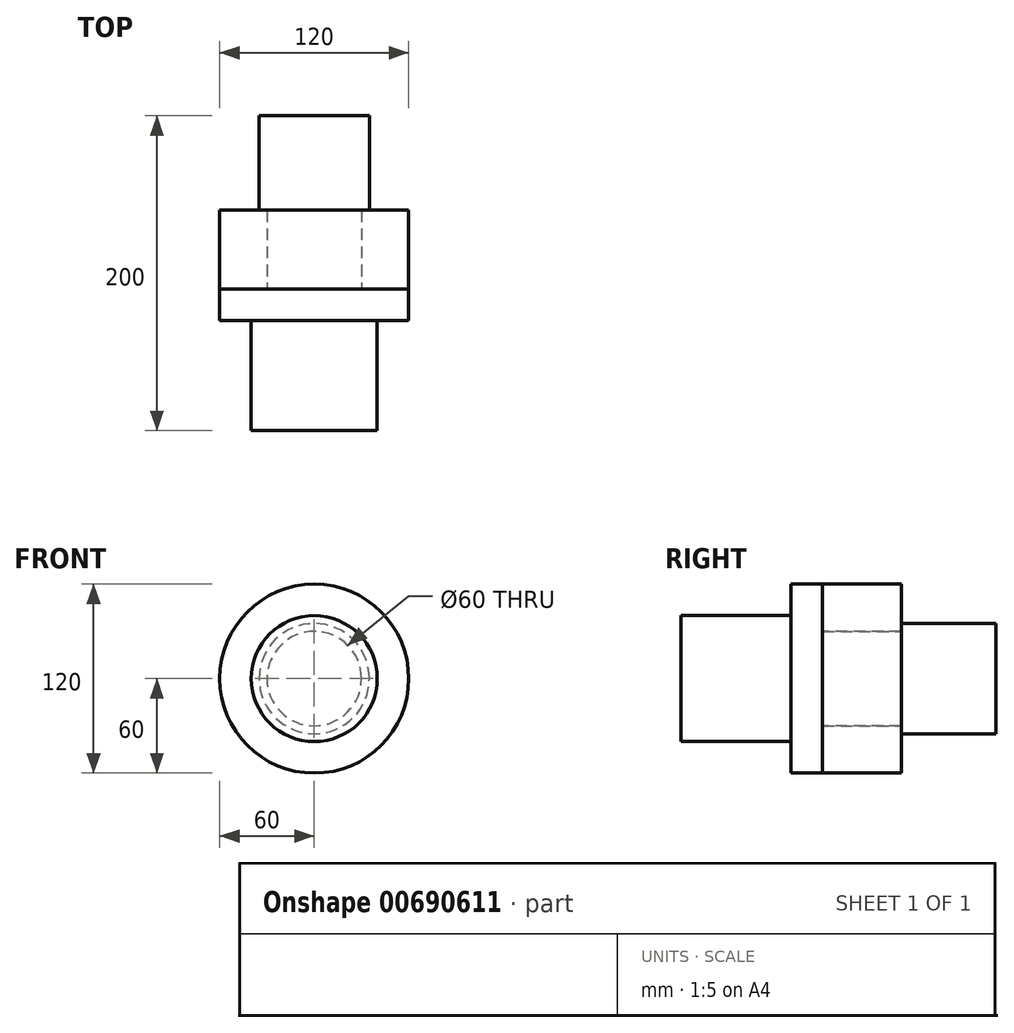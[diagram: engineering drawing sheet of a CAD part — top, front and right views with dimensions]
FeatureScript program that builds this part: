
annotation { "Feature Type Name" : "Feature", "Feature Type Description" : "" }
export const myFeature = defineFeature(function(context is Context, id is Id, definition is map)
    precondition{}
    {
        {
            var Q0;
            Q0=qCreatedBy(makeId("Right.planeOp"),FACE);
            var sketch = newSketch(context, id + "F0", { "sketchPlane" : qUnion([Q0])});
            skLineSegment(sketch, "E0", {"start": v(0, 0) * mm, "end": v(0, 40) * mm});
            skLineSegment(sketch, "E1", {"start": v(0, 40) * mm, "end": v(70, 40) * mm});
            skLineSegment(sketch, "E2", {"start": v(70, 40) * mm, "end": v(70, 60) * mm});
            skLineSegment(sketch, "E3", {"start": v(70, 60) * mm, "end": v(90, 60) * mm});
            skLineSegment(sketch, "E4", {"start": v(90, 60) * mm, "end": v(90, 30) * mm});
            skLineSegment(sketch, "E5", {"start": v(90, 30) * mm, "end": v(140, 30) * mm});
            skLineSegment(sketch, "E6", {"start": v(140, 35) * mm, "end": v(140, 30) * mm});
            skLineSegment(sketch, "E7", {"start": v(140, 35) * mm, "end": v(200, 35) * mm});
            skLineSegment(sketch, "E8", {"start": v(200, 35) * mm, "end": v(200, 0) * mm});
            skLineSegment(sketch, "E9", {"start": v(200, 0) * mm, "end": v(0, 0) * mm});
            skSolve(sketch);
        }
        {
            var Q0;
            Q0=makeQuery(id+"F0.imprint","IMPRINT",FACE,{"disambiguationData":[TD([[makeQuery(id+"F0.imprint","IMPRINT",EDGE,{"derivedFrom":sQuery(id+"F0.wireOp",EDGE,"E0")}),-1.0]])]});
            var Q1;
            Q1=sQuery(id+"F0.wireOp",EDGE,"E9");
            revolve(context, id + "F1", {"entities" : qUnion([Q0]), "axis" : qUnion([Q1]), "revolveType" : RevolveType.FULL});
        }
        {
            var Q0;
            Q0=qCreatedBy(makeId("Top.planeOp"),FACE);
            var sketch = newSketch(context, id + "F2", { "sketchPlane" : qUnion([Q0])});
            skLineSegment(sketch, "E10", {"start": v(30, 140) * mm, "end": v(30, 90) * mm});
            skLineSegment(sketch, "E11", {"start": v(30, 90) * mm, "end": v(60, 90) * mm});
            skLineSegment(sketch, "E12", {"start": v(60, 90) * mm, "end": v(60, 140) * mm});
            skLineSegment(sketch, "E13", {"start": v(60, 140) * mm, "end": v(30, 140) * mm});
            skSolve(sketch);
        }
        {
            var Q0;
            Q0=makeQuery(id+"F2.imprint","IMPRINT",FACE,{"disambiguationData":[TD([[makeQuery(id+"F2.imprint","IMPRINT",EDGE,{"derivedFrom":sQuery(id+"F2.wireOp",EDGE,"E10")}),1.0]])]});
            var Q1;
            Q1=makeQuery(id+"F1.opRevolve","SWEPT_FACE",FACE,{"disambiguationData":[OSD([sQuery(id+"F0.wireOp",EDGE,"E5")])]});
            revolve(context, id + "F3", {"entities" : qUnion([Q0]), "axis" : qUnion([Q1]), "revolveType" : RevolveType.FULL});
        }
    });
